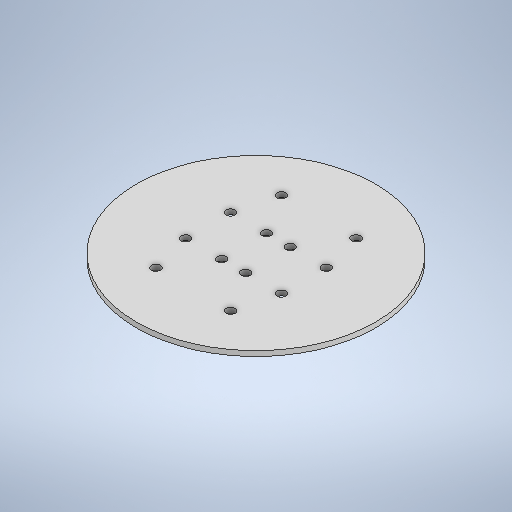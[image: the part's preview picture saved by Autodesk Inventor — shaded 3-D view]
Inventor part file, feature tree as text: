
AUTODESK INVENTOR PART (.ipt)
format: ipt  version: 2025.2 (Build 292293000, 293)  size: 249,344 bytes
history: native  units: mm
features: extrude x1, sketch x1
ambient origin geometry x8: Origin, YZ Plane, XZ Plane, XY Plane, X Axis, Y Axis, Z Axis, Center Point
bodies: Solid1 (feature_tree)
feature tree (2):
  extrude  "Extrusion1"  Depth=1.7mm
  sketch  "Sketch1"  dims[d0=80.0mm d1=3.0mm d2=3.0mm d3=3.0mm d4=4.0mm d5=7.5mm d6=12.0mm d7=0.0mm d8=12.5mm d9=21.0mm d10=1.7mm d11=0.0mm]
